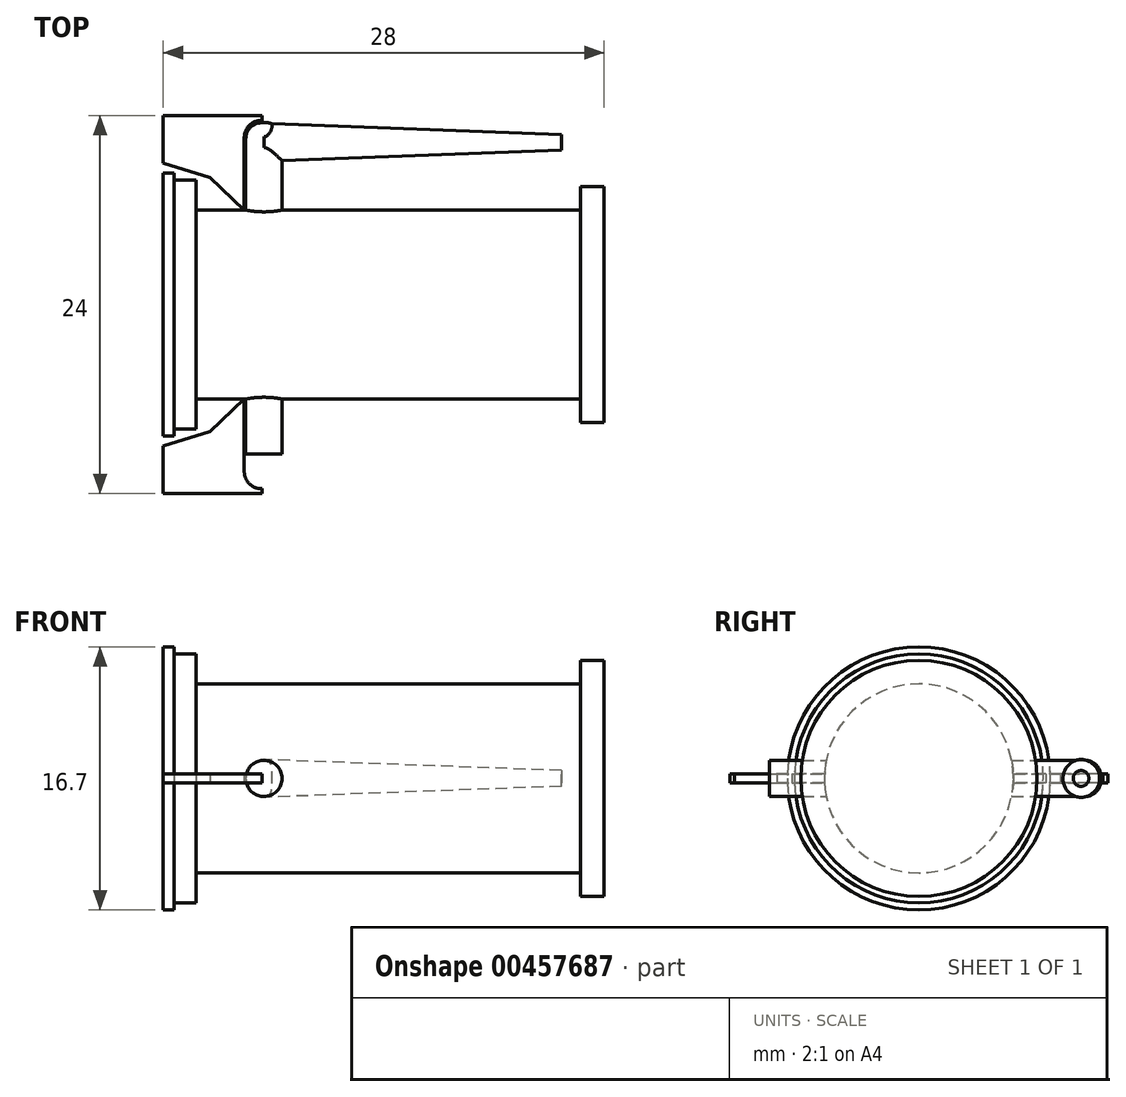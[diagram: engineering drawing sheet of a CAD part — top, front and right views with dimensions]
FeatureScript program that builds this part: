
annotation { "Feature Type Name" : "Feature", "Feature Type Description" : "" }
export const myFeature = defineFeature(function(context is Context, id is Id, definition is map)
    precondition{}
    {
        {
            var Q0;
            Q0=qCreatedBy(makeId("Front.planeOp"),FACE);
            var sketch = newSketch(context, id + "F0", { "sketchPlane" : qUnion([Q0])});
            skLineSegment(sketch, "E0", {"start": v(0, 0) * mm, "end": v(0, 8.5) * mm});
            skLineSegment(sketch, "E1", {"start": v(0, 8.5) * mm, "end": v(0.6, 8.5) * mm});
            skLineSegment(sketch, "E2", {"start": v(0, 0) * mm, "end": v(0, -8.5) * mm});
            skLineSegment(sketch, "E3", {"start": v(0, -8.5) * mm, "end": v(0.55, -8.5) * mm});
            skLineSegment(sketch, "E4", {"start": v(5.18, -5.96) * mm, "end": v(5.18, -10.26) * mm});
            skLineSegment(sketch, "E5", {"start": v(5.18, -10.26) * mm, "end": v(7.58, -10.26) * mm});
            skLineSegment(sketch, "E6", {"start": v(5.2, 5.87) * mm, "end": v(5.2, 11.62) * mm});
            skLineSegment(sketch, "E7", {"start": v(5.2, 11.62) * mm, "end": v(25.3, 10.8) * mm});
            skLineSegment(sketch, "E8", {"start": v(25.3, 10.8) * mm, "end": v(25.3, 9.8) * mm});
            skLineSegment(sketch, "E9", {"start": v(25.3, 9.8) * mm, "end": v(7.58, 9.38) * mm});
            skLineSegment(sketch, "E10", {"start": v(7.58, 9.38) * mm, "end": v(7.58, 5.88) * mm});
            skLineSegment(sketch, "E11", {"start": v(7.58, 5.88) * mm, "end": v(5.2, 5.87) * mm});
            skSolve(sketch);
        }
        {
            var Q0;
            Q0=qCreatedBy(makeId("Front.planeOp"),FACE);
            var sketch = newSketch(context, id + "F1", { "sketchPlane" : qUnion([Q0])});
            skLineSegment(sketch, "E12", {"start": v(0, 0) * mm, "end": v(0, 8.35) * mm});
            skLineSegment(sketch, "E13", {"start": v(0, 8.35) * mm, "end": v(0.7, 8.35) * mm});
            skLineSegment(sketch, "E14", {"start": v(0.7, 8.35) * mm, "end": v(0.7, 7.9) * mm});
            skLineSegment(sketch, "E15", {"start": v(0.7, 7.9) * mm, "end": v(2.1, 7.9) * mm});
            skLineSegment(sketch, "E16", {"start": v(2.1, 7.9) * mm, "end": v(2.1, 6) * mm});
            skLineSegment(sketch, "E17", {"start": v(2.1, 6) * mm, "end": v(26.5, 6) * mm});
            skLineSegment(sketch, "E18", {"start": v(26.5, 6) * mm, "end": v(26.5, 7.5) * mm});
            skLineSegment(sketch, "E19", {"start": v(26.5, 7.5) * mm, "end": v(28, 7.5) * mm});
            skLineSegment(sketch, "E20", {"start": v(28, 7.5) * mm, "end": v(28, 0) * mm});
            skLineSegment(sketch, "E21", {"start": v(28, 0) * mm, "end": v(0, 0) * mm});
            skSolve(sketch);
        }
        {
            var Q0;
            Q0 = qSketchRegion(id + "F1", true);
            var Q1;
            Q1=sQuery(id+"F1.wireOp",EDGE,"E21");
            revolve(context, id + "F2", {"entities" : qUnion([Q0]), "axis" : qUnion([Q1]), "revolveType" : RevolveType.FULL});
        }
        {
            var Q0;
            Q0=qCreatedBy(makeId("Front.planeOp"),FACE);
            var sketch = newSketch(context, id + "F3", { "sketchPlane" : qUnion([Q0])});
            skCircle(sketch, "E22", {"center": v(6.4, 0) * mm, "radius": 1.15 * mm});
            skSolve(sketch);
        }
        {
            var Q0;
            Q0 = qSketchRegion(id + "F3", true);
            extrude(context, id + "F4", {"entities" : qUnion([Q0]), "operationType" : NewBodyOperationType.ADD, "depth" : (3.5 + 6) * mm, "hasSecondDirection" : true, "secondDirectionOppositeDirection" : true, "secondDirectionDepth" : (4.3 + 6 + 1.15 + 0.1) * mm});
        }
        {
            var Q0;
            Q0=qCreatedBy(makeId("Right.planeOp"),FACE);
            cPlane(context, id + "F5", {"entities" : qUnion([Q0]), "cplaneType" : CPlaneType.OFFSET, "offset" : 25.3 * mm, "width" : 150 * mm, "height" : 150 * mm});
        }
        {
            var Q0;
            Q0=qCreatedBy(id+"F5.planeOp",FACE);
            var sketch = newSketch(context, id + "F6", { "sketchPlane" : qUnion([Q0])});
            skCircle(sketch, "E23", {"center": v(10.3, 0) * mm, "radius": 0.5 * mm});
            skSolve(sketch);
        }
        {
            var Q0;
            Q0=qCreatedBy(makeId("Right.planeOp"),FACE);
            cPlane(context, id + "F7", {"entities" : qUnion([Q0]), "cplaneType" : CPlaneType.OFFSET, "offset" : 6.4 * mm, "width" : 150 * mm, "height" : 150 * mm});
        }
        {
            var Q0;
            Q0=qCreatedBy(id+"F7.planeOp",FACE);
            var sketch = newSketch(context, id + "F8", { "sketchPlane" : qUnion([Q0])});
            skCircle(sketch, "E24", {"center": v(10.3, 0) * mm, "radius": 1.2 * mm});
            skSolve(sketch);
        }
        {
            var Q1;
            Q1 = qSketchRegion(id + "F8", true);
            var Q2;
            Q2 = qSketchRegion(id + "F6", true);
            loft(context, id + "F9", {"operationType" : NewBodyOperationType.ADD, "sheetProfilesArray" : [{ "sheetProfileEntities" : qUnion([Q1]) }, { "sheetProfileEntities" : qUnion([Q2]) }]});
        }
        {
            var Q0;
            Q0=makeQuery(id+"F9.boolean.opBoolean","SPLIT",EDGE,{"derivedFrom":makeQuery(id+"F4.opExtrude","CAP_EDGE",EDGE,{"disambiguationData":[OSD([sQuery(id+"F3.wireOp",EDGE,"E22")])],"isStart":true})});
            fillet(context, id + "F10", {"entities" : qUnion([Q0]), "radius" : 1 * mm, "tangentPropagation" : true, "allowEdgeOverflow" : false});
        }
        {
            var Q0;
            Q0=qCreatedBy(makeId("Top.planeOp"),FACE);
            var sketch = newSketch(context, id + "F11", { "sketchPlane" : qUnion([Q0])});
            skLineSegment(sketch, "E25", {"start": v(5.15, 6) * mm, "end": v(5.15, 10.6) * mm});
            skLineSegment(sketch, "E26", {"start": v(0, 11.29) * mm, "end": v(0, 9) * mm});
            skLineSegment(sketch, "E27", {"start": v(0, 9) * mm, "end": v(2.97, 8.05) * mm});
            skLineSegment(sketch, "E28", {"start": v(2.97, 8.05) * mm, "end": v(5.15, 6) * mm});
            skArc(sketch, "E29", {"start": v(6.29, 11.7) * mm, "mid": v(5.49, 11.4) * mm, "end": v(5.15, 10.6) * mm});
            skLineSegment(sketch, "E30", {"start": v(6.29, 11.7) * mm, "end": v(6.29, 12) * mm});
            skLineSegment(sketch, "E31", {"start": v(6.29, 12) * mm, "end": v(0, 12) * mm});
            skLineSegment(sketch, "E32", {"start": v(0, 12) * mm, "end": v(0, 11.29) * mm});
            skSolve(sketch);
        }
        {
            var Q0;
            Q0 = qSketchRegion(id + "F11", true);
            extrude(context, id + "F12", {"entities" : qUnion([Q0]), "endBound" : BoundingType.SYMMETRIC, "depth" : .6 * mm});
        }
        {
            var Q0;
            Q0=makeQuery(id+"F12.opExtrude","SWEPT_BODY",BODY,{"disambiguationData":[OSD([sQuery(id+"F11.wireOp",EDGE,"E25"),sQuery(id+"F11.wireOp",EDGE,"E26"),sQuery(id+"F11.wireOp",EDGE,"E27"),sQuery(id+"F11.wireOp",EDGE,"E28"),sQuery(id+"F11.wireOp",EDGE,"E29"),sQuery(id+"F11.wireOp",EDGE,"E30"),sQuery(id+"F11.wireOp",EDGE,"E31"),sQuery(id+"F11.wireOp",EDGE,"E32")])]});
            var Q1;
            Q1=qCreatedBy(makeId("Front.planeOp"),FACE);
            mirror(context, id + "F13", {"entities" : qUnion([Q0]), "mirrorPlane" : qUnion([Q1])});
        }
    });
